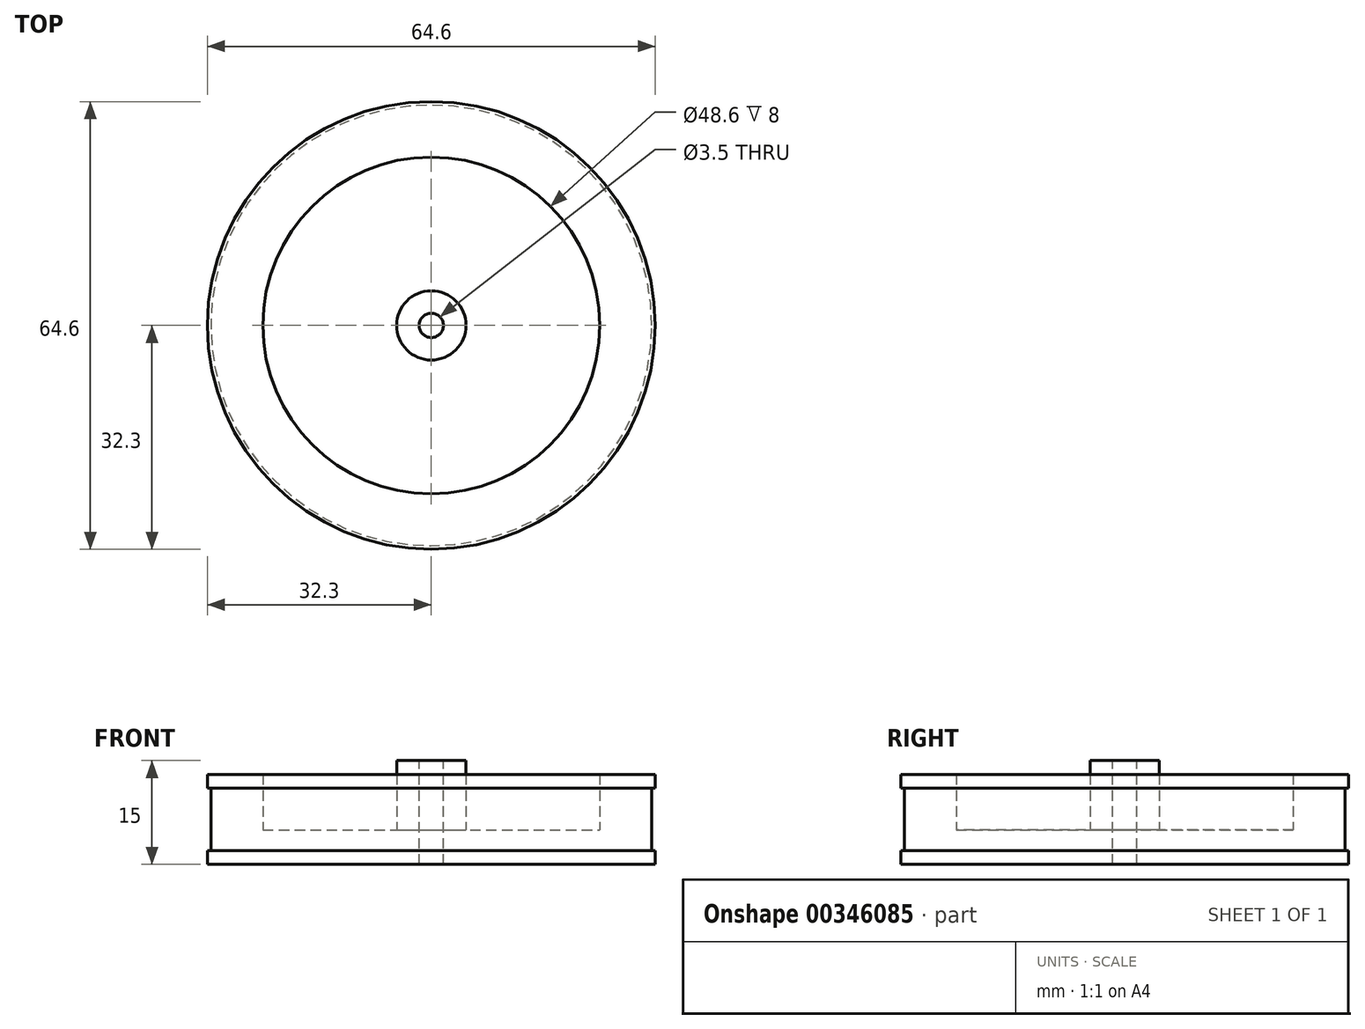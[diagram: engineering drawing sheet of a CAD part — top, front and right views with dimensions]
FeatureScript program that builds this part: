
annotation { "Feature Type Name" : "Feature", "Feature Type Description" : "" }
export const myFeature = defineFeature(function(context is Context, id is Id, definition is map)
    precondition{}
    {
        {
            var Q0;
            Q0=qCreatedBy(makeId("Front.planeOp"),FACE);
            var sketch = newSketch(context, id + "F0", { "sketchPlane" : qUnion([Q0])});
            skLineSegment(sketch, "E0", {"start": v(0, 0) * mm, "end": v(32.3, 0) * mm});
            skLineSegment(sketch, "E1", {"start": v(32.3, 0) * mm, "end": v(32.3, 2) * mm});
            skLineSegment(sketch, "E2", {"start": v(32.3, 2) * mm, "end": v(31.8, 2) * mm});
            skLineSegment(sketch, "E3", {"start": v(31.8, 2) * mm, "end": v(31.8, 11) * mm});
            skLineSegment(sketch, "E4", {"start": v(31.8, 11) * mm, "end": v(32.3, 11) * mm});
            skLineSegment(sketch, "E5", {"start": v(32.3, 11) * mm, "end": v(32.3, 13) * mm});
            skLineSegment(sketch, "E6", {"start": v(32.3, 13) * mm, "end": v(24.3, 13) * mm});
            skLineSegment(sketch, "E7", {"start": v(24.3, 13) * mm, "end": v(24.3, 5) * mm});
            skLineSegment(sketch, "E8", {"start": v(24.3, 5) * mm, "end": v(0, 5) * mm});
            skLineSegment(sketch, "E9", {"start": v(0, 5) * mm, "end": v(0, 0) * mm});
            skLineSegment(sketch, "E10", {"start": v(0, 5) * mm, "end": v(0, 15) * mm});
            skLineSegment(sketch, "E11", {"start": v(0, 15) * mm, "end": v(5, 15) * mm});
            skLineSegment(sketch, "E12", {"start": v(5, 15) * mm, "end": v(5, 5) * mm});
            skSolve(sketch);
        }
        {
            var Q0;
            {var subQ0=sQuery(id+"F0.wireOp",EDGE,"E10");Q0=makeQuery(id+"F0.imprint","IMPRINT",FACE,{"disambiguationData":[TD([[makeQuery(id+"F0.imprint","IMPRINT",EDGE,{"derivedFrom":subQ0}),-1.0]])]});}
            var Q1;
            Q1=makeQuery(id+"F0.imprint","IMPRINT",FACE,{"disambiguationData":[TD([[makeQuery(id+"F0.imprint","IMPRINT",EDGE,{"derivedFrom":sQuery(id+"F0.wireOp",EDGE,"E0")}),1.0]])]});
            var Q2;
            Q2=sQuery(id+"F0.wireOp",EDGE,"E10");
            revolve(context, id + "F1", {"entities" : qUnion([Q0, Q1]), "axis" : qUnion([Q2]), "revolveType" : RevolveType.FULL});
        }
        {
            var Q0;
            Q0=makeQuery(id+"F1.opRevolve","SWEPT_FACE",FACE,{"disambiguationData":[OSD([sQuery(id+"F0.wireOp",EDGE,"E11")])]});
            var sketch = newSketch(context, id + "F2", { "sketchPlane" : qUnion([Q0])});
            skCircle(sketch, "E13.0", {"center": v(0, 0) * mm, "radius": 5 * mm});
            skCircle(sketch, "E14", {"center": v(0, 0) * mm, "radius": 1.75 * mm});
            skSolve(sketch);
        }
        {
            var Q0;
            Q0=makeQuery(id+"F2.imprint","IMPRINT",FACE,{"disambiguationData":[TD([[makeQuery(id+"F2.imprint","IMPRINT",EDGE,{"derivedFrom":sQuery(id+"F2.wireOp",EDGE,"E14")}),1.0]])]});
            extrude(context, id + "F3", {"entities" : qUnion([Q0]), "operationType" : NewBodyOperationType.REMOVE, "oppositeDirection" : true, "depth" : 80 * mm});
        }
    });
